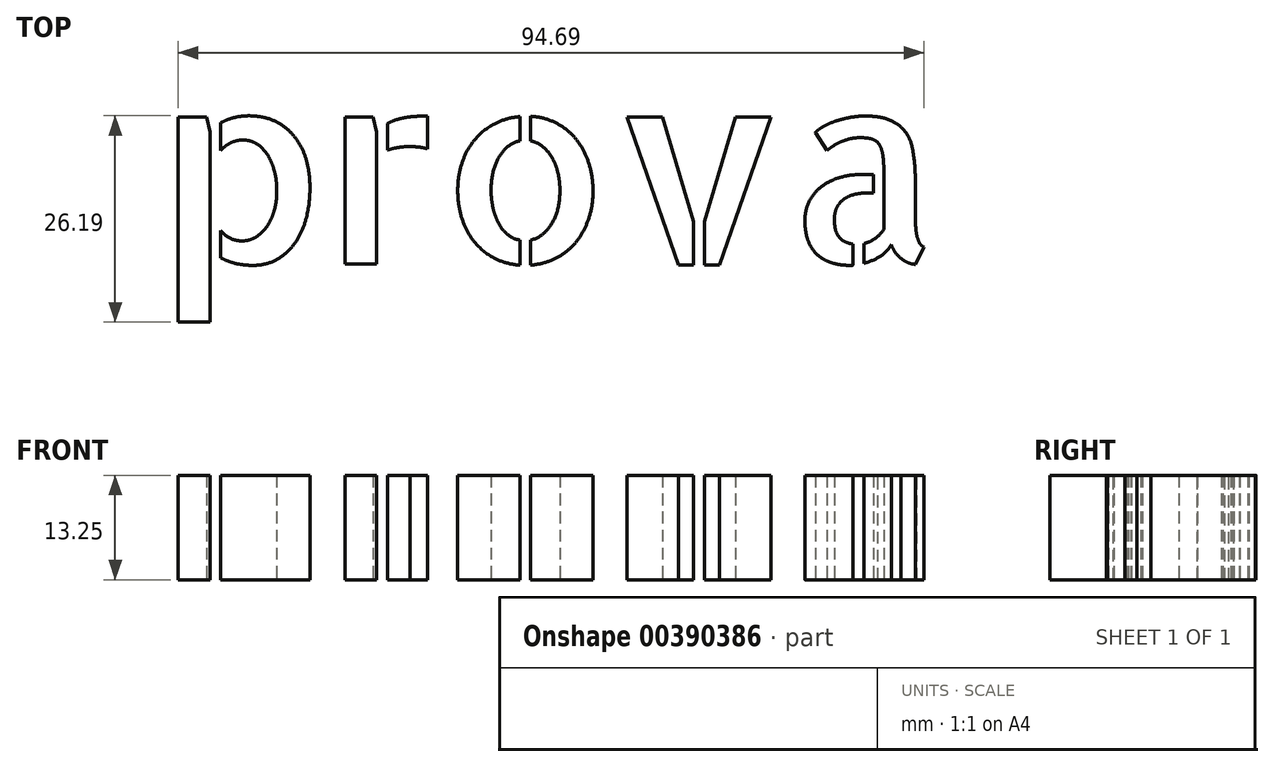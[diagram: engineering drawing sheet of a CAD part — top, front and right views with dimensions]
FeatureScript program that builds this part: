
annotation { "Feature Type Name" : "Feature", "Feature Type Description" : "" }
export const myFeature = defineFeature(function(context is Context, id is Id, definition is map)
    precondition{}
    {
        {
            var Q0;
            Q0=qCreatedBy(makeId("Top.planeOp"),FACE);
            var sketch = newSketch(context, id + "F0", { "sketchPlane" : qUnion([Q0])});
            skText(sketch, "E0", { "text": "prova", "fontName": "AllertaStencil-Regular.ttf"});
            const initialGuessF0  = {"E0": [0.0045, 0, 1, 0, 0.02441]};
            skSetInitialGuess(sketch, initialGuessF0);
            skSolve(sketch);
        }
        {
            var Q0;
            Q0 = qSketchRegion(id + "F0", true);
            extrude(context, id + "F1", {"entities" : qUnion([Q0]), "depth" : 13.25 * mm});
        }
    });
